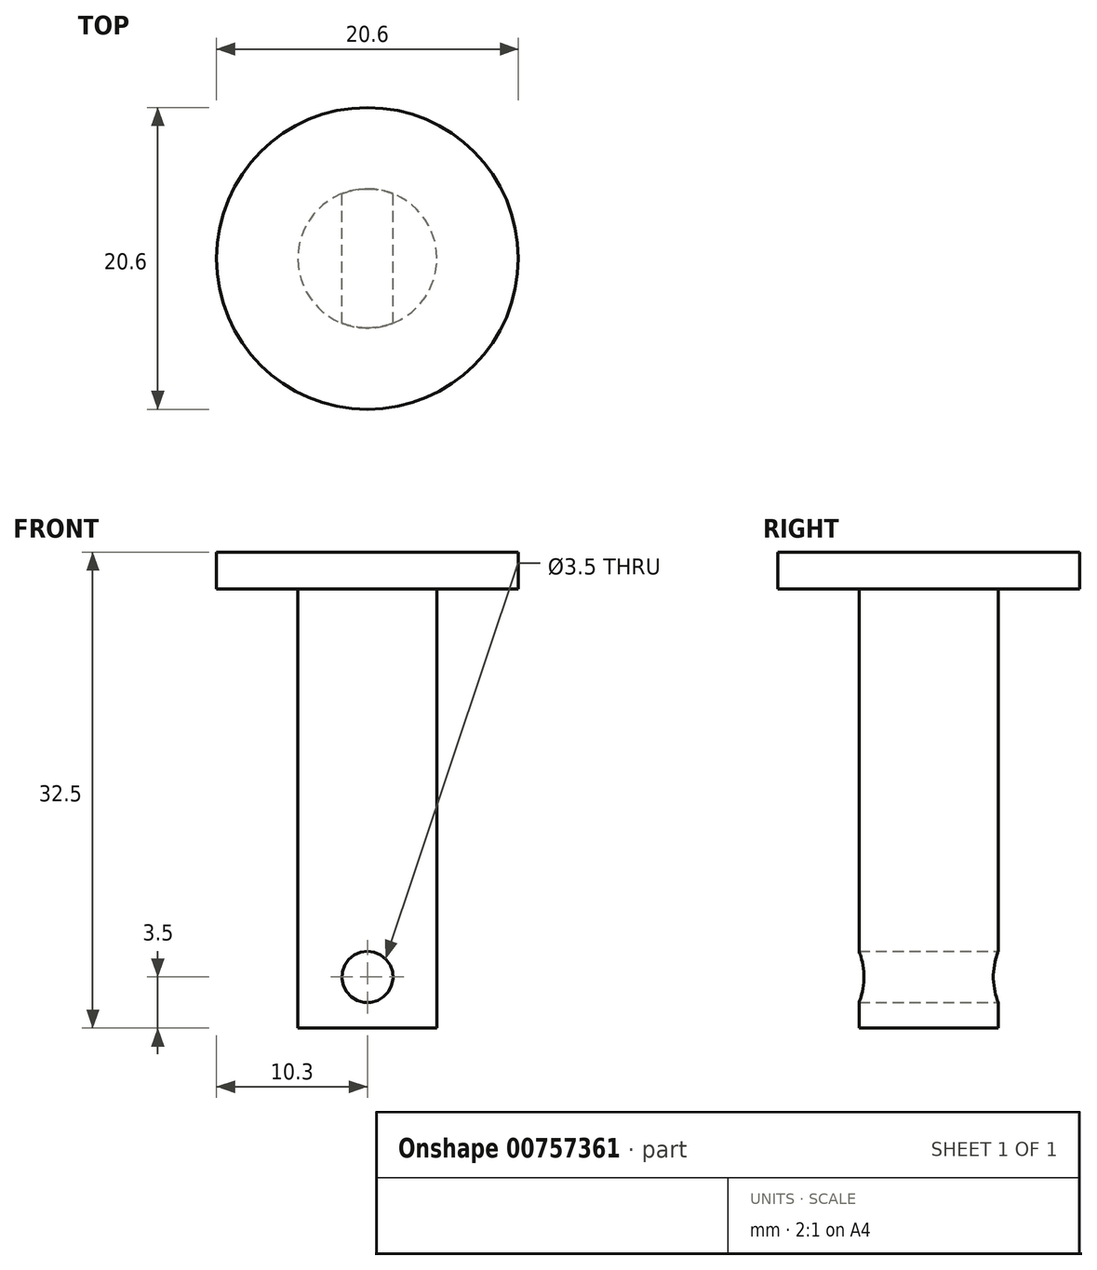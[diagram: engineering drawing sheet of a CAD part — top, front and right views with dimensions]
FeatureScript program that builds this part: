
annotation { "Feature Type Name" : "Feature", "Feature Type Description" : "" }
export const myFeature = defineFeature(function(context is Context, id is Id, definition is map)
    precondition{}
    {
        {
            var Q0;
            Q0=qCreatedBy(makeId("Top.planeOp"),FACE);
            var sketch = newSketch(context, id + "F0", { "sketchPlane" : qUnion([Q0])});
            skCircle(sketch, "E0", {"center": v(0, 0) * mm, "radius": 4.75 * mm});
            skSolve(sketch);
        }
        {
            var Q0;
            Q0 = qSketchRegion(id + "F0", true);
            extrude(context, id + "F1", {"entities" : qUnion([Q0]), "depth" : 30 * mm, "offsetDistance" : 25 * mm});
        }
        {
            var Q0;
            Q0=makeQuery(id+"F1.opExtrude","CAP_FACE",FACE,{"disambiguationData":[OSD([sQuery(id+"F0.wireOp",EDGE,"E0")])],"isStart":false});
            var sketch = newSketch(context, id + "F2", { "sketchPlane" : qUnion([Q0])});
            skCircle(sketch, "E1", {"center": v(0, 0) * mm, "radius": 10.3 * mm});
            skSolve(sketch);
        }
        {
            var Q0;
            Q0 = qSketchRegion(id + "F2", true);
            extrude(context, id + "F3", {"entities" : qUnion([Q0]), "operationType" : NewBodyOperationType.ADD, "depth" : 2.5 * mm, "offsetDistance" : 25 * mm});
        }
        {
            var Q0;
            Q0=qCreatedBy(makeId("Front.planeOp"),FACE);
            var sketch = newSketch(context, id + "F4", { "sketchPlane" : qUnion([Q0])});
            skCircle(sketch, "E2", {"center": v(0, 3.5) * mm, "radius": 1.75 * mm});
            skSolve(sketch);
        }
        {
            var Q0;
            Q0 = qSketchRegion(id + "F4", true);
            extrude(context, id + "F5", {"entities" : qUnion([Q0]), "operationType" : NewBodyOperationType.REMOVE, "endBound" : BoundingType.SYMMETRIC, "depth" : 25 * mm, "offsetDistance" : 25 * mm});
        }
    });
